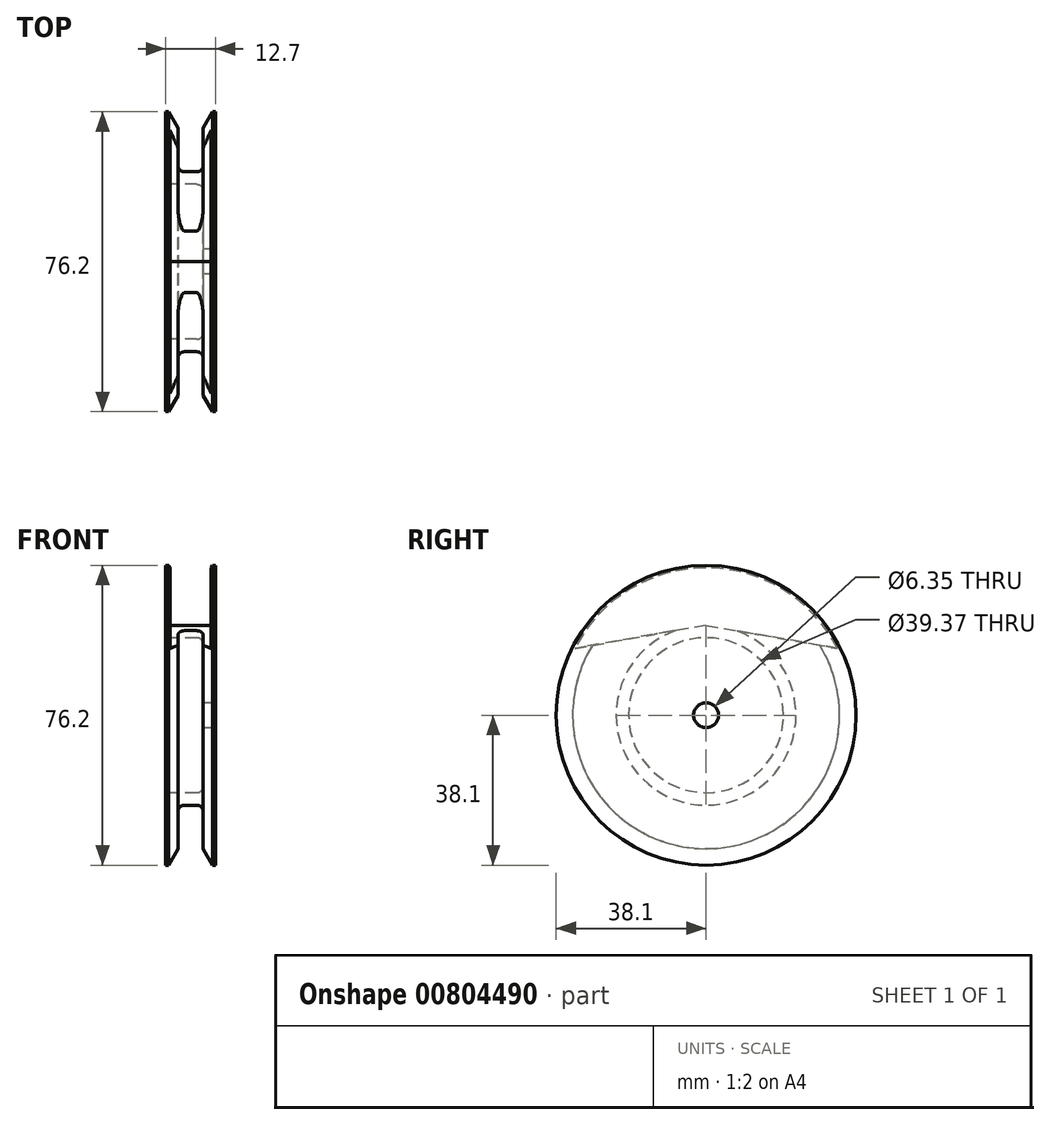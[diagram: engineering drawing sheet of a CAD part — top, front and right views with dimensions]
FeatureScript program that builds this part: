
annotation { "Feature Type Name" : "Feature", "Feature Type Description" : "" }
export const myFeature = defineFeature(function(context is Context, id is Id, definition is map)
    precondition{}
    {
        {
            var Q0;
            Q0=qCreatedBy(makeId("Front.planeOp"),FACE);
            var sketch = newSketch(context, id + "F0", { "sketchPlane" : qUnion([Q0])});
            skLineSegment(sketch, "E0", {"start": v(-6.35, 3.18) * mm, "end": v(6.35, 3.18) * mm});
            skPoint(sketch, "E1", {"position": v(0, 3.18) * mm});
            skLineSegment(sketch, "E2", {"start": v(-6.35, 3.18) * mm, "end": v(-6.35, 38.1) * mm});
            skLineSegment(sketch, "E3", {"start": v(6.35, 3.18) * mm, "end": v(6.35, 38.1) * mm});
            skLineSegment(sketch, "E4", {"start": v(-6.35, 38.1) * mm, "end": v(-5.59, 38.1) * mm});
            skLineSegment(sketch, "E5", {"start": v(-5.59, 38.1) * mm, "end": v(-3.18, 33.92) * mm});
            skLineSegment(sketch, "E6", {"start": v(3.18, 33.92) * mm, "end": v(5.59, 38.1) * mm});
            skLineSegment(sketch, "E7", {"start": v(5.59, 38.1) * mm, "end": v(6.35, 38.1) * mm});
            skLineSegment(sketch, "E8", {"start": v(-3.17, 33.92) * mm, "end": v(-3.17, 22.86) * mm});
            skLineSegment(sketch, "E9", {"start": v(-3.17, 22.86) * mm, "end": v(3.18, 22.86) * mm});
            skLineSegment(sketch, "E10", {"start": v(3.17, 22.86) * mm, "end": v(3.17, 33.92) * mm});
            skLineSegment(sketch, "E11", {"start": v(-6.35, 0) * mm, "end": v(6.35, 0) * mm, "construction": true});
            skSolve(sketch);
        }
        {
            var Q0;
            Q0 = qSketchRegion(id + "F0", true);
            var Q1;
            Q1=sQuery(id+"F0.wireOp",EDGE,"E11");
            revolve(context, id + "F1", {"surfaceOperationType" : NewSurfaceOperationType.NEW, "entities" : qUnion([Q0]), "axis" : qUnion([Q1]), "revolveType" : RevolveType.FULL});
        }
        {
            var Q0;
            Q0=makeQuery(id+"F1.opRevolve","SWEPT_FACE",FACE,{"disambiguationData":[OSD([sQuery(id+"F0.wireOp",EDGE,"E2")])]});
            var sketch = newSketch(context, id + "F2", { "sketchPlane" : qUnion([Q0])});
            skCircle(sketch, "E12", {"center": v(0, 0) * mm, "radius": 19.69 * mm});
            skSolve(sketch);
        }
        {
            var Q0;
            Q0=makeQuery(id+"F2.imprint","IMPRINT",FACE,{"disambiguationData":[TD([[makeQuery(id+"F2.imprint","IMPRINT",EDGE,{"derivedFrom":sQuery(id+"F2.wireOp",EDGE,"E12")}),1.0]])]});
            extrude(context, id + "F3", {"entities" : qUnion([Q0]), "operationType" : NewBodyOperationType.REMOVE, "oppositeDirection" : true, "depth" : 9.52 * mm, "offsetDistance" : 25.4 * mm});
        }
        {
            var Q0;
            Q0=makeQuery(id+"F3.boolean.opBoolean","COPY",EDGE,{"derivedFrom":makeQuery(id+"F3.opExtrude","CAP_EDGE",EDGE,{"disambiguationData":[OSD([sQuery(id+"F2.wireOp",EDGE,"E12")])],"isStart":true})});
            var Q1;
            Q1=makeQuery(id+"F3.boolean.opBoolean","COPY",EDGE,{"derivedFrom":makeQuery(id+"F3.opExtrude","CAP_EDGE",EDGE,{"disambiguationData":[OSD([sQuery(id+"F2.wireOp",EDGE,"E12")])],"isStart":false})});
            var Q2;
            Q2=makeQuery(id+"F1.opRevolve","SWEPT_EDGE",EDGE,{"disambiguationData":[OSD([sQuery(id+"F0.wireOp",EDGE,"E8"),sQuery(id+"F0.wireOp",EDGE,"E9")])]});
            var Q3;
            Q3=makeQuery(id+"F1.opRevolve","SWEPT_EDGE",EDGE,{"disambiguationData":[OSD([sQuery(id+"F0.wireOp",EDGE,"E9"),sQuery(id+"F0.wireOp",EDGE,"E10")])]});
            fillet(context, id + "F4", {"entities" : qUnion([Q0, Q1, Q2, Q3]), "radius" : 1.59 * mm, "tangentPropagation" : true, "allowEdgeOverflow" : false});
        }
        {
            var Q0;
            Q0=qCreatedBy(makeId("Right.planeOp"),FACE);
            var sketch = newSketch(context, id + "F5", { "sketchPlane" : qUnion([Q0])});
            skLineSegment(sketch, "E13", {"start": v(0, 22.86) * mm, "end": v(-34.18, 16.83) * mm});
            skLineSegment(sketch, "E14", {"start": v(0, 22.86) * mm, "end": v(34.18, 16.83) * mm});
            skLineSegment(sketch, "E15", {"start": v(34.18, 16.83) * mm, "end": v(34.18, 38.1) * mm});
            skLineSegment(sketch, "E16", {"start": v(34.18, 38.1) * mm, "end": v(-34.18, 38.1) * mm});
            skLineSegment(sketch, "E17", {"start": v(-34.18, 38.1) * mm, "end": v(-34.18, 16.83) * mm});
            skSolve(sketch);
        }
        {
            var Q0;
            Q0=makeQuery(id+"F5.imprint","IMPRINT",FACE,{"disambiguationData":[TD([[makeQuery(id+"F5.imprint","IMPRINT",EDGE,{"derivedFrom":sQuery(id+"F5.wireOp",EDGE,"E13")}),-1.0]])]});
            extrude(context, id + "F6", {"entities" : qUnion([Q0]), "operationType" : NewBodyOperationType.REMOVE, "endBound" : BoundingType.SYMMETRIC, "oppositeDirection" : true, "depth" : 10.4 * mm, "offsetDistance" : 25.4 * mm});
        }
    });
